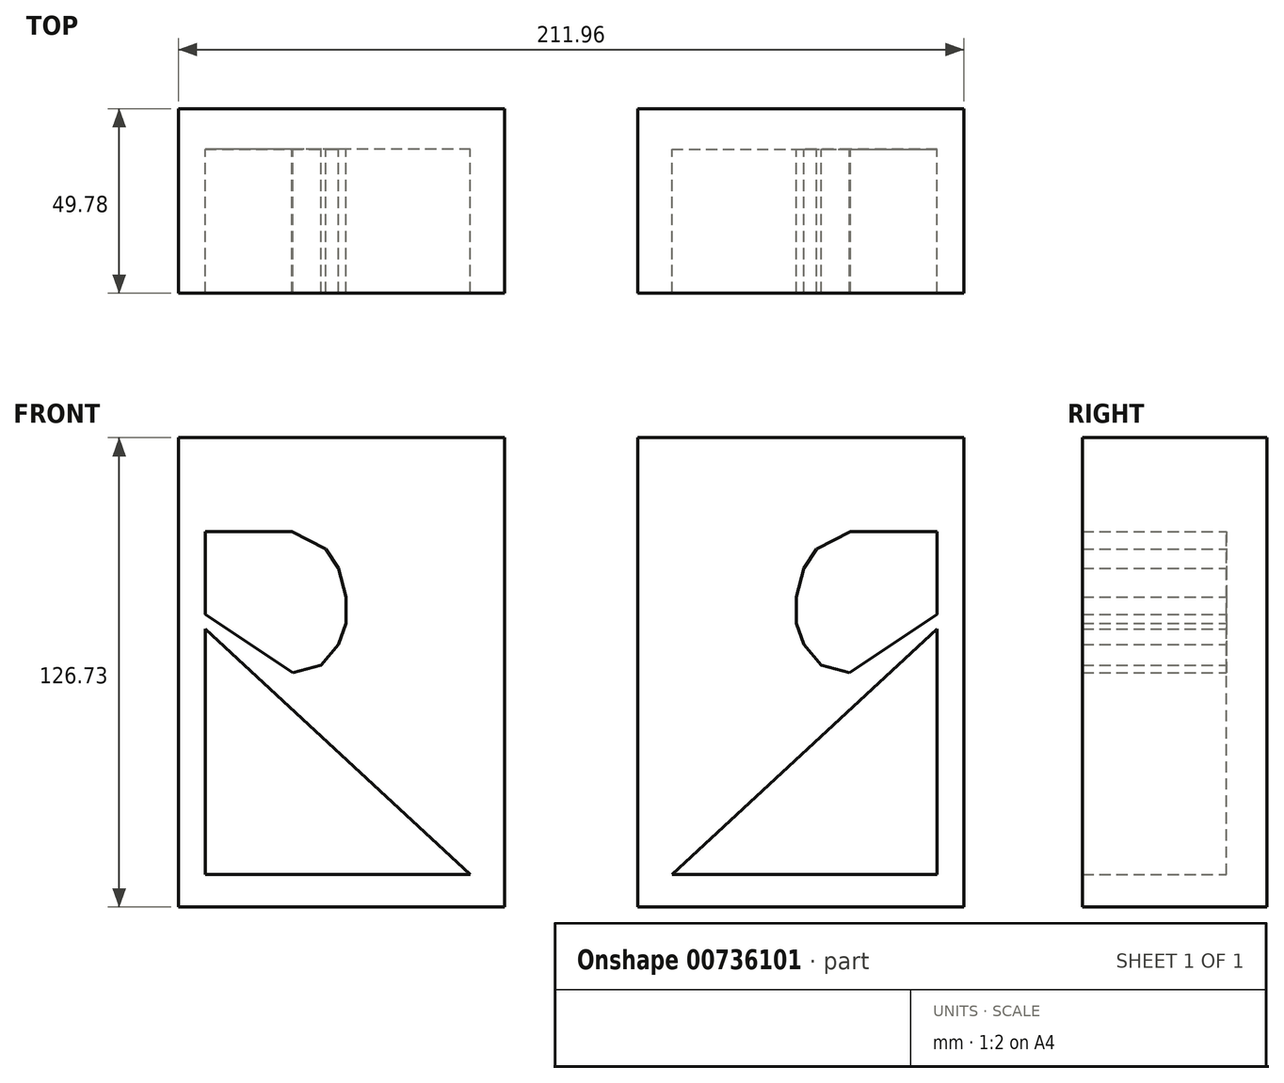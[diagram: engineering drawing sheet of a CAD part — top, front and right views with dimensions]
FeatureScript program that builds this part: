
annotation { "Feature Type Name" : "Feature", "Feature Type Description" : "" }
export const myFeature = defineFeature(function(context is Context, id is Id, definition is map)
    precondition{}
    {
        {
            var Q0;
            Q0=qCreatedBy(makeId("Front.planeOp"),FACE);
            var sketch = newSketch(context, id + "F0", { "sketchPlane" : qUnion([Q0])});
            skLineSegment(sketch, "E0.bottom", {"start": v(-105.98, 61.5) * mm, "end": v(-18.01, 61.5) * mm});
            skLineSegment(sketch, "E0.top", {"start": v(-105.98, -65.23) * mm, "end": v(-18.01, -65.23) * mm});
            skLineSegment(sketch, "E0.left", {"start": v(-105.98, 61.5) * mm, "end": v(-105.98, -65.23) * mm});
            skLineSegment(sketch, "E0.right", {"start": v(-18.01, 61.5) * mm, "end": v(-18.01, -65.23) * mm});
            skSolve(sketch);
        }
        {
            var Q0;
            Q0 = qSketchRegion(id + "F0", true);
            extrude(context, id + "F1", {"entities" : qUnion([Q0]), "depth" : 49.78 * mm, "offsetDistance" : 25.4 * mm});
        }
        {
            var Q0;
            Q0=qCreatedBy(makeId("Front.planeOp"),FACE);
            var sketch = newSketch(context, id + "F2", { "sketchPlane" : qUnion([Q0])});
            skLineSegment(sketch, "E1", {"start": v(-98.77, 9.81) * mm, "end": v(-98.77, -56.53) * mm});
            skLineSegment(sketch, "E2", {"start": v(-98.77, -56.53) * mm, "end": v(-27.2, -56.53) * mm});
            skLineSegment(sketch, "E3", {"start": v(-27.2, -56.53) * mm, "end": v(-98.77, 9.81) * mm});
            skLineSegment(sketch, "E4", {"start": v(-98.77, 13.8) * mm, "end": v(-98.77, 36.15) * mm});
            skLineSegment(sketch, "E5", {"start": v(-98.77, 36.15) * mm, "end": v(-75.41, 36.15) * mm});
            skLineSegment(sketch, "E6", {"start": v(-75.41, 36.15) * mm, "end": v(-66.22, 31.43) * mm});
            skLineSegment(sketch, "E7", {"start": v(-66.22, 31.43) * mm, "end": v(-62.74, 26.21) * mm});
            skLineSegment(sketch, "E8", {"start": v(-62.74, 26.21) * mm, "end": v(-60.75, 18.51) * mm});
            skLineSegment(sketch, "E9", {"start": v(-60.75, 18.51) * mm, "end": v(-60.75, 11.3) * mm});
            skLineSegment(sketch, "E10", {"start": v(-60.75, 11.3) * mm, "end": v(-62.74, 5.6) * mm});
            skLineSegment(sketch, "E11", {"start": v(-62.74, 5.6) * mm, "end": v(-67.46, 0) * mm});
            skLineSegment(sketch, "E12", {"start": v(-67.46, 0) * mm, "end": v(-75.13, -1.98) * mm});
            skLineSegment(sketch, "E13", {"start": v(-75.13, -1.98) * mm, "end": v(-98.77, 13.8) * mm});
            skSolve(sketch);
        }
        {
            var Q0;
            Q0 = qSketchRegion(id + "F2", true);
            extrude(context, id + "F3", {"entities" : qUnion([Q0]), "operationType" : NewBodyOperationType.REMOVE, "depth" : 70.61 * mm, "offsetDistance" : 25.4 * mm, "hasSecondDirection" : true, "secondDirectionOppositeDirection" : false, "secondDirectionDepth" : 10.92 * mm});
        }
        {
            var Q0;
            Q0=makeQuery(id+"F1.opExtrude","SWEPT_BODY",BODY,{"disambiguationData":[OSD([sQuery(id+"F0.wireOp",EDGE,"E0.bottom"),sQuery(id+"F0.wireOp",EDGE,"E0.top"),sQuery(id+"F0.wireOp",EDGE,"E0.left"),sQuery(id+"F0.wireOp",EDGE,"E0.right")])]});
            var Q1;
            Q1=qCreatedBy(makeId("Right.planeOp"),FACE);
            mirror(context, id + "F4", {"entities" : qUnion([Q0]), "mirrorPlane" : qUnion([Q1])});
        }
    });
